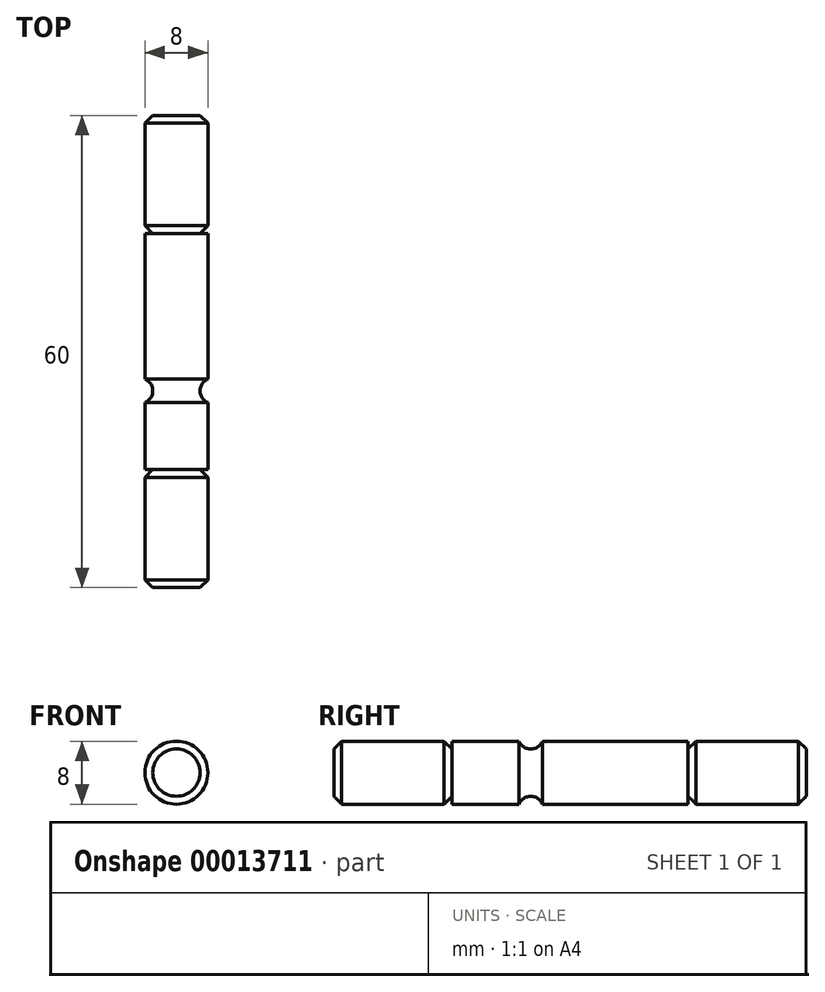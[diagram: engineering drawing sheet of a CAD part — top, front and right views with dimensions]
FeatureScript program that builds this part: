
annotation { "Feature Type Name" : "Feature", "Feature Type Description" : "" }
export const myFeature = defineFeature(function(context is Context, id is Id, definition is map)
    precondition{}
    {
        {
            var Q0;
            Q0=qCreatedBy(makeId("Top.planeOp"),FACE);
            var sketch = newSketch(context, id + "F0", { "sketchPlane" : qUnion([Q0])});
            skLineSegment(sketch, "E0.rect.bottom", {"start": v(3, 30) * mm, "end": v(-4, 30) * mm});
            skLineSegment(sketch, "E0.rect.top", {"start": v(3, -30) * mm, "end": v(-4, -30) * mm});
            skLineSegment(sketch, "E0.rect.left", {"start": v(4, 29) * mm, "end": v(4, 16) * mm});
            skLineSegment(sketch, "E0.rect.right", {"start": v(-4, 30) * mm, "end": v(-4, -30) * mm});
            skPoint(sketch, "E0.rect.middle", {"position": v(0, 0) * mm});
            skArc(sketch, "E1", {"start": v(4, -3.52) * mm, "mid": v(3, -5) * mm, "end": v(4, -6.48) * mm});
            skArc(sketch, "E2", {"start": v(-4, -6.48) * mm, "mid": v(-3, -5) * mm, "end": v(-4, -3.52) * mm});
            skLineSegment(sketch, "E3", {"start": v(-4.6, -5) * mm, "end": v(4.6, -5) * mm, "construction": true});
            skLineSegment(sketch, "E4", {"start": v(0, -30) * mm, "end": v(0, -5) * mm});
            skLineSegment(sketch, "E5", {"start": v(-4, -15) * mm, "end": v(4, -15) * mm});
            skLineSegment(sketch, "E6", {"start": v(-4, 15) * mm, "end": v(4, 15) * mm});
            skLineSegment(sketch, "E7", {"start": v(3, 30) * mm, "end": v(4, 29) * mm});
            skLineSegment(sketch, "E8", {"start": v(3, -30) * mm, "end": v(4, -29) * mm});
            skLineSegment(sketch, "E9", {"start": v(0, -5) * mm, "end": v(0, 30) * mm});
            skPoint(sketch, "E10.orphan", {"position": v(4, -30) * mm});
            skPoint(sketch, "E11.orphan", {"position": v(4, 30) * mm});
            skLineSegment(sketch, "E12", {"start": v(3, -15) * mm, "end": v(4, -16) * mm});
            skLineSegment(sketch, "E13", {"start": v(4, 16) * mm, "end": v(3, 15) * mm});
            skLineSegment(sketch, "E14.trimOffspring", {"start": v(4, 15) * mm, "end": v(4, -15) * mm});
            skLineSegment(sketch, "E15.trimOffspring", {"start": v(4, -16) * mm, "end": v(4, -29) * mm});
            skSolve(sketch);
        }
        {
            var Q0;
            Q0=makeQuery(id+"F0.imprint","IMPRINT",FACE,{"disambiguationData":[TD([[makeQuery(id+"F0.imprint","IMPRINT",EDGE,{"derivedFrom":sQuery(id+"F0.wireOp",EDGE,"E0.rect.left")}),-1.0]])]});
            var Q1;
            {var subQ3=sQuery(id+"F0.wireOp",EDGE,"E1");Q1=makeQuery(id+"F0.imprint","IMPRINT",FACE,{"disambiguationData":[TD([[makeQuery(id+"F0.imprint","IMPRINT",EDGE,{"derivedFrom":subQ3}),-1.0]])]});}
            var Q2;
            {var subQ1=sQuery(id+"F0.wireOp",EDGE,"E8");Q2=makeQuery(id+"F0.imprint","IMPRINT",FACE,{"disambiguationData":[TD([[makeQuery(id+"F0.imprint","IMPRINT",EDGE,{"derivedFrom":subQ1}),1.0]])]});}
            var Q3;
            Q3=sQuery(id+"F0.wireOp",EDGE,"E4");
            revolve(context, id + "F1", {"entities" : qUnion([Q0, Q1, Q2]), "axis" : qUnion([Q3]), "revolveType" : RevolveType.FULL});
        }
    });
